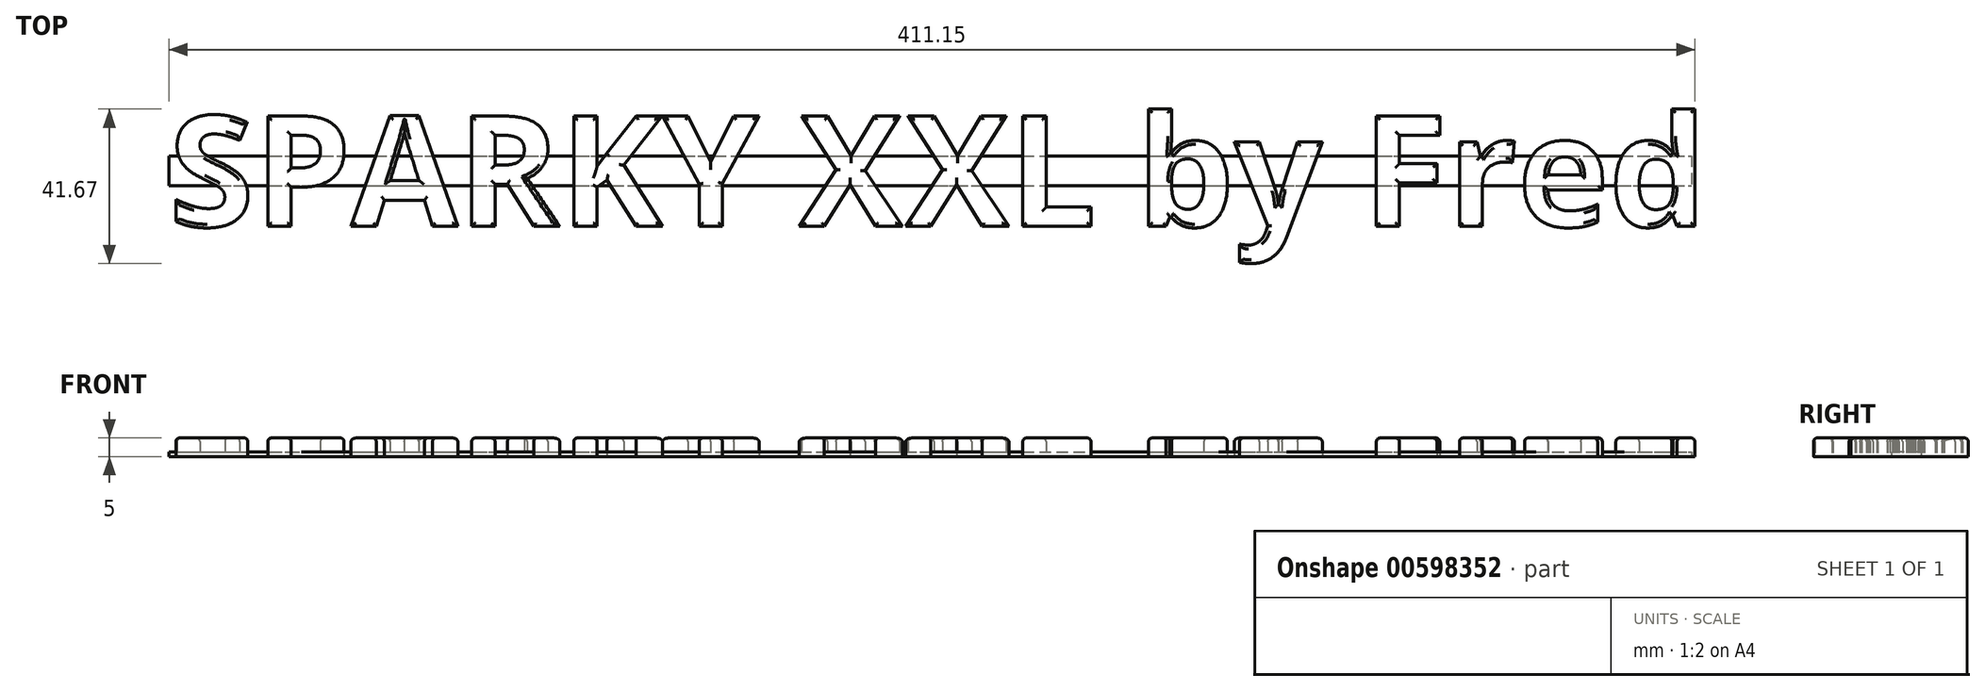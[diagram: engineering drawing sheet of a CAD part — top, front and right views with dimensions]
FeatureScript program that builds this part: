
annotation { "Feature Type Name" : "Feature", "Feature Type Description" : "" }
export const myFeature = defineFeature(function(context is Context, id is Id, definition is map)
    precondition{}
    {
        {
            var Q0;
            Q0=qCreatedBy(makeId("Top.planeOp"),FACE);
            var sketch = newSketch(context, id + "F0", { "sketchPlane" : qUnion([Q0])});
            skText(sketch, "E0", { "text": "SPARKY XXL by Fred", "fontName": "OpenSans-Bold.ttf"});
            const initialGuessF0  = {"E0": [0, 0, 1, 0, 0.03]};
            skSetInitialGuess(sketch, initialGuessF0);
            skSolve(sketch);
        }
        {
            var Q0;
            Q0 = qSketchRegion(id + "F0", true);
            extrude(context, id + "F1", {"entities" : qUnion([Q0]), "depth" : 5 * mm, "offsetDistance" : 25 * mm});
        }
        {
            var Q0;
            Q0=makeQuery(id+"F1.opExtrude","CAP_FACE",FACE,{"disambiguationData":[OSD([sQuery(id+"F0.wireOp",EDGE,"E0.sketch_text.stroke-0"),sQuery(id+"F0.wireOp",EDGE,"E0.sketch_text.stroke-1"),sQuery(id+"F0.wireOp",EDGE,"E0.sketch_text.stroke-2"),sQuery(id+"F0.wireOp",EDGE,"E0.sketch_text.stroke-3"),sQuery(id+"F0.wireOp",EDGE,"E0.sketch_text.stroke-4"),sQuery(id+"F0.wireOp",EDGE,"E0.sketch_text.stroke-5"),sQuery(id+"F0.wireOp",EDGE,"E0.sketch_text.stroke-6"),sQuery(id+"F0.wireOp",EDGE,"E0.sketch_text.stroke-7"),sQuery(id+"F0.wireOp",EDGE,"E0.sketch_text.stroke-8"),sQuery(id+"F0.wireOp",EDGE,"E0.sketch_text.stroke-9"),sQuery(id+"F0.wireOp",EDGE,"E0.sketch_text.stroke-10"),sQuery(id+"F0.wireOp",EDGE,"E0.sketch_text.stroke-11"),sQuery(id+"F0.wireOp",EDGE,"E0.sketch_text.stroke-12"),sQuery(id+"F0.wireOp",EDGE,"E0.sketch_text.stroke-13"),sQuery(id+"F0.wireOp",EDGE,"E0.sketch_text.stroke-14"),sQuery(id+"F0.wireOp",EDGE,"E0.sketch_text.stroke-15"),sQuery(id+"F0.wireOp",EDGE,"E0.sketch_text.stroke-16"),sQuery(id+"F0.wireOp",EDGE,"E0.sketch_text.stroke-17"),sQuery(id+"F0.wireOp",EDGE,"E0.sketch_text.stroke-18"),sQuery(id+"F0.wireOp",EDGE,"E0.sketch_text.stroke-19"),sQuery(id+"F0.wireOp",EDGE,"E0.sketch_text.stroke-20"),sQuery(id+"F0.wireOp",EDGE,"E0.sketch_text.stroke-21"),sQuery(id+"F0.wireOp",EDGE,"E0.sketch_text.stroke-22"),sQuery(id+"F0.wireOp",EDGE,"E0.sketch_text.stroke-23"),sQuery(id+"F0.wireOp",EDGE,"E0.sketch_text.stroke-24"),sQuery(id+"F0.wireOp",EDGE,"E0.sketch_text.stroke-25"),sQuery(id+"F0.wireOp",EDGE,"E0.sketch_text.stroke-26"),sQuery(id+"F0.wireOp",EDGE,"E0.sketch_text.stroke-27")])],"isStart":false});
            var Q1;
            Q1=makeQuery(id+"F1.opExtrude","CAP_FACE",FACE,{"disambiguationData":[OSD([sQuery(id+"F0.wireOp",EDGE,"E0.sketch_text.stroke-28"),sQuery(id+"F0.wireOp",EDGE,"E0.sketch_text.stroke-29"),sQuery(id+"F0.wireOp",EDGE,"E0.sketch_text.stroke-30"),sQuery(id+"F0.wireOp",EDGE,"E0.sketch_text.stroke-31"),sQuery(id+"F0.wireOp",EDGE,"E0.sketch_text.stroke-32"),sQuery(id+"F0.wireOp",EDGE,"E0.sketch_text.stroke-33"),sQuery(id+"F0.wireOp",EDGE,"E0.sketch_text.stroke-34"),sQuery(id+"F0.wireOp",EDGE,"E0.sketch_text.stroke-35"),sQuery(id+"F0.wireOp",EDGE,"E0.sketch_text.stroke-36"),sQuery(id+"F0.wireOp",EDGE,"E0.sketch_text.stroke-37"),sQuery(id+"F0.wireOp",EDGE,"E0.sketch_text.stroke-38"),sQuery(id+"F0.wireOp",EDGE,"E0.sketch_text.stroke-39"),sQuery(id+"F0.wireOp",EDGE,"E0.sketch_text.stroke-40"),sQuery(id+"F0.wireOp",EDGE,"E0.sketch_text.stroke-41"),sQuery(id+"F0.wireOp",EDGE,"E0.sketch_text.stroke-42"),sQuery(id+"F0.wireOp",EDGE,"E0.sketch_text.stroke-43")])],"isStart":false});
            var Q2;
            Q2=makeQuery(id+"F1.opExtrude","CAP_FACE",FACE,{"disambiguationData":[OSD([sQuery(id+"F0.wireOp",EDGE,"E0.sketch_text.stroke-44"),sQuery(id+"F0.wireOp",EDGE,"E0.sketch_text.stroke-45"),sQuery(id+"F0.wireOp",EDGE,"E0.sketch_text.stroke-46"),sQuery(id+"F0.wireOp",EDGE,"E0.sketch_text.stroke-47"),sQuery(id+"F0.wireOp",EDGE,"E0.sketch_text.stroke-48"),sQuery(id+"F0.wireOp",EDGE,"E0.sketch_text.stroke-49"),sQuery(id+"F0.wireOp",EDGE,"E0.sketch_text.stroke-50"),sQuery(id+"F0.wireOp",EDGE,"E0.sketch_text.stroke-51"),sQuery(id+"F0.wireOp",EDGE,"E0.sketch_text.stroke-52"),sQuery(id+"F0.wireOp",EDGE,"E0.sketch_text.stroke-53"),sQuery(id+"F0.wireOp",EDGE,"E0.sketch_text.stroke-54"),sQuery(id+"F0.wireOp",EDGE,"E0.sketch_text.stroke-55")])],"isStart":false});
            var Q3;
            Q3=makeQuery(id+"F1.opExtrude","CAP_FACE",FACE,{"disambiguationData":[OSD([sQuery(id+"F0.wireOp",EDGE,"E0.sketch_text.stroke-56"),sQuery(id+"F0.wireOp",EDGE,"E0.sketch_text.stroke-57"),sQuery(id+"F0.wireOp",EDGE,"E0.sketch_text.stroke-58"),sQuery(id+"F0.wireOp",EDGE,"E0.sketch_text.stroke-59"),sQuery(id+"F0.wireOp",EDGE,"E0.sketch_text.stroke-60"),sQuery(id+"F0.wireOp",EDGE,"E0.sketch_text.stroke-61"),sQuery(id+"F0.wireOp",EDGE,"E0.sketch_text.stroke-62"),sQuery(id+"F0.wireOp",EDGE,"E0.sketch_text.stroke-63"),sQuery(id+"F0.wireOp",EDGE,"E0.sketch_text.stroke-64"),sQuery(id+"F0.wireOp",EDGE,"E0.sketch_text.stroke-65"),sQuery(id+"F0.wireOp",EDGE,"E0.sketch_text.stroke-66"),sQuery(id+"F0.wireOp",EDGE,"E0.sketch_text.stroke-67"),sQuery(id+"F0.wireOp",EDGE,"E0.sketch_text.stroke-68"),sQuery(id+"F0.wireOp",EDGE,"E0.sketch_text.stroke-69"),sQuery(id+"F0.wireOp",EDGE,"E0.sketch_text.stroke-70"),sQuery(id+"F0.wireOp",EDGE,"E0.sketch_text.stroke-71"),sQuery(id+"F0.wireOp",EDGE,"E0.sketch_text.stroke-72"),sQuery(id+"F0.wireOp",EDGE,"E0.sketch_text.stroke-73"),sQuery(id+"F0.wireOp",EDGE,"E0.sketch_text.stroke-74")])],"isStart":false});
            var Q4;
            Q4=makeQuery(id+"F1.opExtrude","CAP_FACE",FACE,{"disambiguationData":[OSD([sQuery(id+"F0.wireOp",EDGE,"E0.sketch_text.stroke-75"),sQuery(id+"F0.wireOp",EDGE,"E0.sketch_text.stroke-76"),sQuery(id+"F0.wireOp",EDGE,"E0.sketch_text.stroke-77"),sQuery(id+"F0.wireOp",EDGE,"E0.sketch_text.stroke-78"),sQuery(id+"F0.wireOp",EDGE,"E0.sketch_text.stroke-79"),sQuery(id+"F0.wireOp",EDGE,"E0.sketch_text.stroke-80"),sQuery(id+"F0.wireOp",EDGE,"E0.sketch_text.stroke-81"),sQuery(id+"F0.wireOp",EDGE,"E0.sketch_text.stroke-82"),sQuery(id+"F0.wireOp",EDGE,"E0.sketch_text.stroke-83"),sQuery(id+"F0.wireOp",EDGE,"E0.sketch_text.stroke-84"),sQuery(id+"F0.wireOp",EDGE,"E0.sketch_text.stroke-85"),sQuery(id+"F0.wireOp",EDGE,"E0.sketch_text.stroke-86"),sQuery(id+"F0.wireOp",EDGE,"E0.sketch_text.stroke-87")])],"isStart":false});
            var Q5;
            Q5=makeQuery(id+"F1.opExtrude","CAP_FACE",FACE,{"disambiguationData":[OSD([sQuery(id+"F0.wireOp",EDGE,"E0.sketch_text.stroke-88"),sQuery(id+"F0.wireOp",EDGE,"E0.sketch_text.stroke-89"),sQuery(id+"F0.wireOp",EDGE,"E0.sketch_text.stroke-90"),sQuery(id+"F0.wireOp",EDGE,"E0.sketch_text.stroke-91"),sQuery(id+"F0.wireOp",EDGE,"E0.sketch_text.stroke-92"),sQuery(id+"F0.wireOp",EDGE,"E0.sketch_text.stroke-93"),sQuery(id+"F0.wireOp",EDGE,"E0.sketch_text.stroke-94"),sQuery(id+"F0.wireOp",EDGE,"E0.sketch_text.stroke-95"),sQuery(id+"F0.wireOp",EDGE,"E0.sketch_text.stroke-96")])],"isStart":false});
            var Q6;
            Q6=makeQuery(id+"F1.opExtrude","CAP_FACE",FACE,{"disambiguationData":[OSD([sQuery(id+"F0.wireOp",EDGE,"E0.sketch_text.stroke-97"),sQuery(id+"F0.wireOp",EDGE,"E0.sketch_text.stroke-98"),sQuery(id+"F0.wireOp",EDGE,"E0.sketch_text.stroke-99"),sQuery(id+"F0.wireOp",EDGE,"E0.sketch_text.stroke-100"),sQuery(id+"F0.wireOp",EDGE,"E0.sketch_text.stroke-101"),sQuery(id+"F0.wireOp",EDGE,"E0.sketch_text.stroke-102"),sQuery(id+"F0.wireOp",EDGE,"E0.sketch_text.stroke-103"),sQuery(id+"F0.wireOp",EDGE,"E0.sketch_text.stroke-104"),sQuery(id+"F0.wireOp",EDGE,"E0.sketch_text.stroke-105"),sQuery(id+"F0.wireOp",EDGE,"E0.sketch_text.stroke-106"),sQuery(id+"F0.wireOp",EDGE,"E0.sketch_text.stroke-107"),sQuery(id+"F0.wireOp",EDGE,"E0.sketch_text.stroke-108")])],"isStart":false});
            var Q7;
            Q7=makeQuery(id+"F1.opExtrude","CAP_FACE",FACE,{"disambiguationData":[OSD([sQuery(id+"F0.wireOp",EDGE,"E0.sketch_text.stroke-109"),sQuery(id+"F0.wireOp",EDGE,"E0.sketch_text.stroke-110"),sQuery(id+"F0.wireOp",EDGE,"E0.sketch_text.stroke-111"),sQuery(id+"F0.wireOp",EDGE,"E0.sketch_text.stroke-112"),sQuery(id+"F0.wireOp",EDGE,"E0.sketch_text.stroke-113"),sQuery(id+"F0.wireOp",EDGE,"E0.sketch_text.stroke-114"),sQuery(id+"F0.wireOp",EDGE,"E0.sketch_text.stroke-115"),sQuery(id+"F0.wireOp",EDGE,"E0.sketch_text.stroke-116"),sQuery(id+"F0.wireOp",EDGE,"E0.sketch_text.stroke-117"),sQuery(id+"F0.wireOp",EDGE,"E0.sketch_text.stroke-118"),sQuery(id+"F0.wireOp",EDGE,"E0.sketch_text.stroke-119"),sQuery(id+"F0.wireOp",EDGE,"E0.sketch_text.stroke-120")])],"isStart":false});
            var Q8;
            Q8=makeQuery(id+"F1.opExtrude","CAP_FACE",FACE,{"disambiguationData":[OSD([sQuery(id+"F0.wireOp",EDGE,"E0.sketch_text.stroke-121"),sQuery(id+"F0.wireOp",EDGE,"E0.sketch_text.stroke-122"),sQuery(id+"F0.wireOp",EDGE,"E0.sketch_text.stroke-123"),sQuery(id+"F0.wireOp",EDGE,"E0.sketch_text.stroke-124"),sQuery(id+"F0.wireOp",EDGE,"E0.sketch_text.stroke-125"),sQuery(id+"F0.wireOp",EDGE,"E0.sketch_text.stroke-126")])],"isStart":false});
            var Q9;
            Q9=makeQuery(id+"F1.opExtrude","CAP_FACE",FACE,{"disambiguationData":[OSD([sQuery(id+"F0.wireOp",EDGE,"E0.sketch_text.stroke-127"),sQuery(id+"F0.wireOp",EDGE,"E0.sketch_text.stroke-128"),sQuery(id+"F0.wireOp",EDGE,"E0.sketch_text.stroke-129"),sQuery(id+"F0.wireOp",EDGE,"E0.sketch_text.stroke-130"),sQuery(id+"F0.wireOp",EDGE,"E0.sketch_text.stroke-131"),sQuery(id+"F0.wireOp",EDGE,"E0.sketch_text.stroke-132"),sQuery(id+"F0.wireOp",EDGE,"E0.sketch_text.stroke-133"),sQuery(id+"F0.wireOp",EDGE,"E0.sketch_text.stroke-134"),sQuery(id+"F0.wireOp",EDGE,"E0.sketch_text.stroke-135"),sQuery(id+"F0.wireOp",EDGE,"E0.sketch_text.stroke-136"),sQuery(id+"F0.wireOp",EDGE,"E0.sketch_text.stroke-137"),sQuery(id+"F0.wireOp",EDGE,"E0.sketch_text.stroke-138"),sQuery(id+"F0.wireOp",EDGE,"E0.sketch_text.stroke-139"),sQuery(id+"F0.wireOp",EDGE,"E0.sketch_text.stroke-140"),sQuery(id+"F0.wireOp",EDGE,"E0.sketch_text.stroke-141"),sQuery(id+"F0.wireOp",EDGE,"E0.sketch_text.stroke-142"),sQuery(id+"F0.wireOp",EDGE,"E0.sketch_text.stroke-143"),sQuery(id+"F0.wireOp",EDGE,"E0.sketch_text.stroke-144"),sQuery(id+"F0.wireOp",EDGE,"E0.sketch_text.stroke-145"),sQuery(id+"F0.wireOp",EDGE,"E0.sketch_text.stroke-146"),sQuery(id+"F0.wireOp",EDGE,"E0.sketch_text.stroke-147"),sQuery(id+"F0.wireOp",EDGE,"E0.sketch_text.stroke-148"),sQuery(id+"F0.wireOp",EDGE,"E0.sketch_text.stroke-149")])],"isStart":false});
            var Q10;
            Q10=makeQuery(id+"F1.opExtrude","CAP_FACE",FACE,{"disambiguationData":[OSD([sQuery(id+"F0.wireOp",EDGE,"E0.sketch_text.stroke-150"),sQuery(id+"F0.wireOp",EDGE,"E0.sketch_text.stroke-151"),sQuery(id+"F0.wireOp",EDGE,"E0.sketch_text.stroke-152"),sQuery(id+"F0.wireOp",EDGE,"E0.sketch_text.stroke-153"),sQuery(id+"F0.wireOp",EDGE,"E0.sketch_text.stroke-154"),sQuery(id+"F0.wireOp",EDGE,"E0.sketch_text.stroke-155"),sQuery(id+"F0.wireOp",EDGE,"E0.sketch_text.stroke-156"),sQuery(id+"F0.wireOp",EDGE,"E0.sketch_text.stroke-157"),sQuery(id+"F0.wireOp",EDGE,"E0.sketch_text.stroke-158"),sQuery(id+"F0.wireOp",EDGE,"E0.sketch_text.stroke-159"),sQuery(id+"F0.wireOp",EDGE,"E0.sketch_text.stroke-160"),sQuery(id+"F0.wireOp",EDGE,"E0.sketch_text.stroke-161"),sQuery(id+"F0.wireOp",EDGE,"E0.sketch_text.stroke-162"),sQuery(id+"F0.wireOp",EDGE,"E0.sketch_text.stroke-163"),sQuery(id+"F0.wireOp",EDGE,"E0.sketch_text.stroke-164"),sQuery(id+"F0.wireOp",EDGE,"E0.sketch_text.stroke-165"),sQuery(id+"F0.wireOp",EDGE,"E0.sketch_text.stroke-166")])],"isStart":false});
            var Q11;
            Q11=makeQuery(id+"F1.opExtrude","CAP_FACE",FACE,{"disambiguationData":[OSD([sQuery(id+"F0.wireOp",EDGE,"E0.sketch_text.stroke-167"),sQuery(id+"F0.wireOp",EDGE,"E0.sketch_text.stroke-168"),sQuery(id+"F0.wireOp",EDGE,"E0.sketch_text.stroke-169"),sQuery(id+"F0.wireOp",EDGE,"E0.sketch_text.stroke-170"),sQuery(id+"F0.wireOp",EDGE,"E0.sketch_text.stroke-171"),sQuery(id+"F0.wireOp",EDGE,"E0.sketch_text.stroke-172"),sQuery(id+"F0.wireOp",EDGE,"E0.sketch_text.stroke-173"),sQuery(id+"F0.wireOp",EDGE,"E0.sketch_text.stroke-174"),sQuery(id+"F0.wireOp",EDGE,"E0.sketch_text.stroke-175"),sQuery(id+"F0.wireOp",EDGE,"E0.sketch_text.stroke-176")])],"isStart":false});
            var Q12;
            Q12=makeQuery(id+"F1.opExtrude","CAP_FACE",FACE,{"disambiguationData":[OSD([sQuery(id+"F0.wireOp",EDGE,"E0.sketch_text.stroke-177"),sQuery(id+"F0.wireOp",EDGE,"E0.sketch_text.stroke-178"),sQuery(id+"F0.wireOp",EDGE,"E0.sketch_text.stroke-179"),sQuery(id+"F0.wireOp",EDGE,"E0.sketch_text.stroke-180"),sQuery(id+"F0.wireOp",EDGE,"E0.sketch_text.stroke-181"),sQuery(id+"F0.wireOp",EDGE,"E0.sketch_text.stroke-182"),sQuery(id+"F0.wireOp",EDGE,"E0.sketch_text.stroke-183"),sQuery(id+"F0.wireOp",EDGE,"E0.sketch_text.stroke-184"),sQuery(id+"F0.wireOp",EDGE,"E0.sketch_text.stroke-185"),sQuery(id+"F0.wireOp",EDGE,"E0.sketch_text.stroke-186"),sQuery(id+"F0.wireOp",EDGE,"E0.sketch_text.stroke-187"),sQuery(id+"F0.wireOp",EDGE,"E0.sketch_text.stroke-188"),sQuery(id+"F0.wireOp",EDGE,"E0.sketch_text.stroke-189")])],"isStart":false});
            var Q13;
            Q13=makeQuery(id+"F1.opExtrude","CAP_FACE",FACE,{"disambiguationData":[OSD([sQuery(id+"F0.wireOp",EDGE,"E0.sketch_text.stroke-190"),sQuery(id+"F0.wireOp",EDGE,"E0.sketch_text.stroke-191"),sQuery(id+"F0.wireOp",EDGE,"E0.sketch_text.stroke-192"),sQuery(id+"F0.wireOp",EDGE,"E0.sketch_text.stroke-193"),sQuery(id+"F0.wireOp",EDGE,"E0.sketch_text.stroke-194"),sQuery(id+"F0.wireOp",EDGE,"E0.sketch_text.stroke-195"),sQuery(id+"F0.wireOp",EDGE,"E0.sketch_text.stroke-196"),sQuery(id+"F0.wireOp",EDGE,"E0.sketch_text.stroke-197"),sQuery(id+"F0.wireOp",EDGE,"E0.sketch_text.stroke-198"),sQuery(id+"F0.wireOp",EDGE,"E0.sketch_text.stroke-199"),sQuery(id+"F0.wireOp",EDGE,"E0.sketch_text.stroke-200"),sQuery(id+"F0.wireOp",EDGE,"E0.sketch_text.stroke-201"),sQuery(id+"F0.wireOp",EDGE,"E0.sketch_text.stroke-202"),sQuery(id+"F0.wireOp",EDGE,"E0.sketch_text.stroke-203"),sQuery(id+"F0.wireOp",EDGE,"E0.sketch_text.stroke-204"),sQuery(id+"F0.wireOp",EDGE,"E0.sketch_text.stroke-205"),sQuery(id+"F0.wireOp",EDGE,"E0.sketch_text.stroke-206"),sQuery(id+"F0.wireOp",EDGE,"E0.sketch_text.stroke-207"),sQuery(id+"F0.wireOp",EDGE,"E0.sketch_text.stroke-208"),sQuery(id+"F0.wireOp",EDGE,"E0.sketch_text.stroke-209")])],"isStart":false});
            var Q14;
            Q14=makeQuery(id+"F1.opExtrude","CAP_FACE",FACE,{"disambiguationData":[OSD([sQuery(id+"F0.wireOp",EDGE,"E0.sketch_text.stroke-210"),sQuery(id+"F0.wireOp",EDGE,"E0.sketch_text.stroke-211"),sQuery(id+"F0.wireOp",EDGE,"E0.sketch_text.stroke-212"),sQuery(id+"F0.wireOp",EDGE,"E0.sketch_text.stroke-213"),sQuery(id+"F0.wireOp",EDGE,"E0.sketch_text.stroke-214"),sQuery(id+"F0.wireOp",EDGE,"E0.sketch_text.stroke-215"),sQuery(id+"F0.wireOp",EDGE,"E0.sketch_text.stroke-216"),sQuery(id+"F0.wireOp",EDGE,"E0.sketch_text.stroke-217"),sQuery(id+"F0.wireOp",EDGE,"E0.sketch_text.stroke-218"),sQuery(id+"F0.wireOp",EDGE,"E0.sketch_text.stroke-219"),sQuery(id+"F0.wireOp",EDGE,"E0.sketch_text.stroke-220"),sQuery(id+"F0.wireOp",EDGE,"E0.sketch_text.stroke-221"),sQuery(id+"F0.wireOp",EDGE,"E0.sketch_text.stroke-222"),sQuery(id+"F0.wireOp",EDGE,"E0.sketch_text.stroke-223"),sQuery(id+"F0.wireOp",EDGE,"E0.sketch_text.stroke-224"),sQuery(id+"F0.wireOp",EDGE,"E0.sketch_text.stroke-225"),sQuery(id+"F0.wireOp",EDGE,"E0.sketch_text.stroke-226"),sQuery(id+"F0.wireOp",EDGE,"E0.sketch_text.stroke-227"),sQuery(id+"F0.wireOp",EDGE,"E0.sketch_text.stroke-228"),sQuery(id+"F0.wireOp",EDGE,"E0.sketch_text.stroke-229"),sQuery(id+"F0.wireOp",EDGE,"E0.sketch_text.stroke-230"),sQuery(id+"F0.wireOp",EDGE,"E0.sketch_text.stroke-231"),sQuery(id+"F0.wireOp",EDGE,"E0.sketch_text.stroke-232")])],"isStart":false});
            fillet(context, id + "F2", {"entities" : qUnion([Q0, Q1, Q2, Q3, Q4, Q5, Q6, Q7, Q8, Q9, Q10, Q11, Q12, Q13, Q14]), "radius" : 1 * mm, "tangentPropagation" : true, "allowEdgeOverflow" : false});
        }
        {
            var Q0;
            Q0=qCreatedBy(makeId("Top.planeOp"),FACE);
            var sketch = newSketch(context, id + "F3", { "sketchPlane" : qUnion([Q0])});
            skLineSegment(sketch, "E1.bottom", {"start": v(0, 19) * mm, "end": v(410.26, 19) * mm});
            skLineSegment(sketch, "E1.top", {"start": v(0, 11) * mm, "end": v(410.26, 11) * mm});
            skLineSegment(sketch, "E1.left", {"start": v(0, 19) * mm, "end": v(0, 11) * mm});
            skLineSegment(sketch, "E1.right", {"start": v(410.26, 19) * mm, "end": v(410.26, 11) * mm});
            skSolve(sketch);
        }
        {
            var Q0;
            Q0 = qSketchRegion(id + "F3", true);
            extrude(context, id + "F4", {"entities" : qUnion([Q0]), "depth" : 1.2 * mm, "offsetDistance" : 25 * mm});
        }
    });
